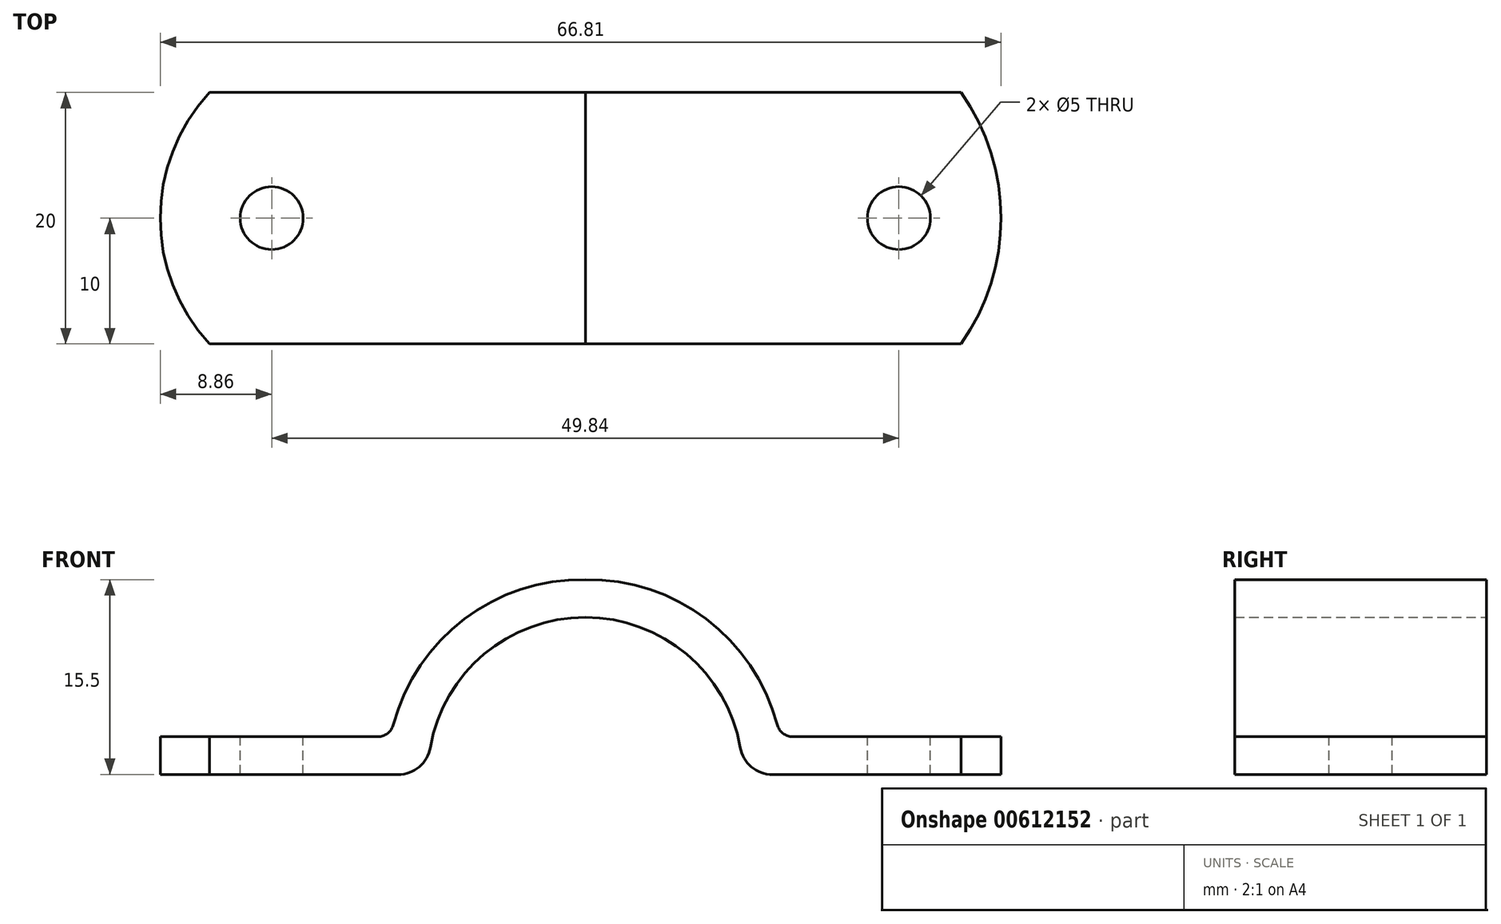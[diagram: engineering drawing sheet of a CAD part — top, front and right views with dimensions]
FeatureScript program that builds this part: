
annotation { "Feature Type Name" : "Feature", "Feature Type Description" : "" }
export const myFeature = defineFeature(function(context is Context, id is Id, definition is map)
    precondition{}
    {
        {
            var Q0;
            Q0=qCreatedBy(makeId("Front.planeOp"),FACE);
            var sketch = newSketch(context, id + "F0", { "sketchPlane" : qUnion([Q0])});
            skLineSegment(sketch, "E0", {"start": v(0, 0) * mm, "end": v(12.5, 0) * mm, "construction": true});
            skLineSegment(sketch, "E1", {"start": v(0, 0) * mm, "end": v(0, 15.5) * mm, "construction": true});
            skLineSegment(sketch, "E2", {"start": v(0, 0) * mm, "end": v(-12.5, 0) * mm, "construction": true});
            skArc(sketch, "E3", {"start": v(12.31, 2.15) * mm, "mid": v(0, 12.5) * mm, "end": v(-12.31, 2.15) * mm});
            skArc(sketch, "E4", {"start": v(15.25, 3.97) * mm, "mid": v(9.61, 12.36) * mm, "end": v(0, 15.5) * mm});
            skArc(sketch, "E5", {"start": v(0, 15.5) * mm, "mid": v(-9.61, 12.36) * mm, "end": v(-15.25, 3.97) * mm});
            skLineSegment(sketch, "E6", {"start": v(-14.87, 0) * mm, "end": v(-29.85, 0) * mm});
            skLineSegment(sketch, "E7", {"start": v(-29.85, 0) * mm, "end": v(-29.85, 3) * mm});
            skLineSegment(sketch, "E8", {"start": v(-29.85, 3) * mm, "end": v(-16.5, 3) * mm});
            skLineSegment(sketch, "E9", {"start": v(14.87, 0) * mm, "end": v(29.85, 0) * mm});
            skLineSegment(sketch, "E10", {"start": v(29.85, 0) * mm, "end": v(29.85, 3) * mm});
            skLineSegment(sketch, "E11", {"start": v(29.85, 3) * mm, "end": v(16.5, 3) * mm});
            skPoint(sketch, "E12.visualSharp", {"position": v(-15.47, 3) * mm});
            skArc(sketch, "E12.filletArc", {"start": v(-16.5, 3) * mm, "mid": v(-15.71, 3.27) * mm, "end": v(-15.25, 3.97) * mm});
            skPoint(sketch, "E13.visualSharp", {"position": v(15.47, 3) * mm});
            skArc(sketch, "E13.filletArc", {"start": v(15.25, 3.97) * mm, "mid": v(15.71, 3.27) * mm, "end": v(16.5, 3) * mm});
            skPoint(sketch, "E14.visualSharp", {"position": v(-12.5, 0) * mm});
            skArc(sketch, "E14.filletArc", {"start": v(-14.87, 0) * mm, "mid": v(-13.2, 0.6) * mm, "end": v(-12.31, 2.15) * mm});
            skPoint(sketch, "E15.visualSharp", {"position": v(12.5, 0) * mm});
            skArc(sketch, "E15.filletArc", {"start": v(12.31, 2.15) * mm, "mid": v(13.2, 0.6) * mm, "end": v(14.87, 0) * mm});
            skSolve(sketch);
        }
        {
            var Q0;
            Q0=makeQuery(id+"F0.imprint","IMPRINT",FACE,{"disambiguationData":[TD([[makeQuery(id+"F0.imprint","IMPRINT",EDGE,{"derivedFrom":sQuery(id+"F0.wireOp",EDGE,"E3")}),-1.0]])]});
            extrude(context, id + "F1", {"entities" : qUnion([Q0]), "endBound" : BoundingType.SYMMETRIC, "depth" : 20 * mm, "offsetDistance" : 25 * mm});
        }
        {
            var Q0;
            Q0=makeQuery(id+"F1.opExtrude","SWEPT_FACE",FACE,{"disambiguationData":[OSD([sQuery(id+"F0.wireOp",EDGE,"E8")])]});
            var sketch = newSketch(context, id + "F2", { "sketchPlane" : qUnion([Q0])});
            skCircle(sketch, "E16", {"center": v(-24.92, 0) * mm, "radius": 2.5 * mm});
            skCircle(sketch, "E17", {"center": v(24.92, 0) * mm, "radius": 2.5 * mm});
            skSolve(sketch);
        }
        {
            var Q0;
            Q0=makeQuery(id+"F2.imprint","IMPRINT",FACE,{"disambiguationData":[TD([[makeQuery(id+"F2.imprint","IMPRINT",EDGE,{"derivedFrom":sQuery(id+"F2.wireOp",EDGE,"E17")}),1.0]])]});
            var Q1;
            Q1=makeQuery(id+"F2.imprint","IMPRINT",FACE,{"disambiguationData":[TD([[makeQuery(id+"F2.imprint","IMPRINT",EDGE,{"derivedFrom":sQuery(id+"F2.wireOp",EDGE,"E16")}),1.0]])]});
            extrude(context, id + "F3", {"entities" : qUnion([Q0, Q1]), "operationType" : NewBodyOperationType.REMOVE, "oppositeDirection" : true, "depth" : 25 * mm, "offsetDistance" : 25 * mm});
        }
        {
            var Q0;
            Q0=makeQuery(id+"F1.opExtrude","SWEPT_FACE",FACE,{"disambiguationData":[OSD([sQuery(id+"F0.wireOp",EDGE,"E8")])]});
            var sketch = newSketch(context, id + "F4", { "sketchPlane" : qUnion([Q0])});
            skArc(sketch, "E18", {"start": v(-29.85, 10) * mm, "mid": v(-33.78, 0) * mm, "end": v(-29.85, -10) * mm});
            skSolve(sketch);
        }
        {
            var Q0;
            Q0=makeQuery(id+"F4.imprint","IMPRINT",FACE,{"disambiguationData":[TD([[makeQuery(id+"F4.imprint","IMPRINT",EDGE,{"derivedFrom":sQuery(id+"F4.wireOp",EDGE,"E18")}),1.0]])]});
            extrude(context, id + "F5", {"entities" : qUnion([Q0]), "operationType" : NewBodyOperationType.ADD, "oppositeDirection" : true, "depth" : 3 * mm, "offsetDistance" : 25 * mm});
        }
        {
            var Q0;
            Q0=makeQuery(id+"F1.opExtrude","SWEPT_FACE",FACE,{"disambiguationData":[OSD([sQuery(id+"F0.wireOp",EDGE,"E11")])]});
            var sketch = newSketch(context, id + "F6", { "sketchPlane" : qUnion([Q0])});
            skArc(sketch, "E19", {"start": v(29.85, -10) * mm, "mid": v(33.03, 0) * mm, "end": v(29.85, 10) * mm});
            skSolve(sketch);
        }
        {
            var Q0;
            Q0=makeQuery(id+"F6.imprint","IMPRINT",FACE,{"disambiguationData":[TD([[makeQuery(id+"F6.imprint","IMPRINT",EDGE,{"derivedFrom":sQuery(id+"F6.wireOp",EDGE,"E19")}),1.0]])]});
            extrude(context, id + "F7", {"entities" : qUnion([Q0]), "operationType" : NewBodyOperationType.ADD, "oppositeDirection" : true, "depth" : 3 * mm, "offsetDistance" : 25 * mm});
        }
    });
